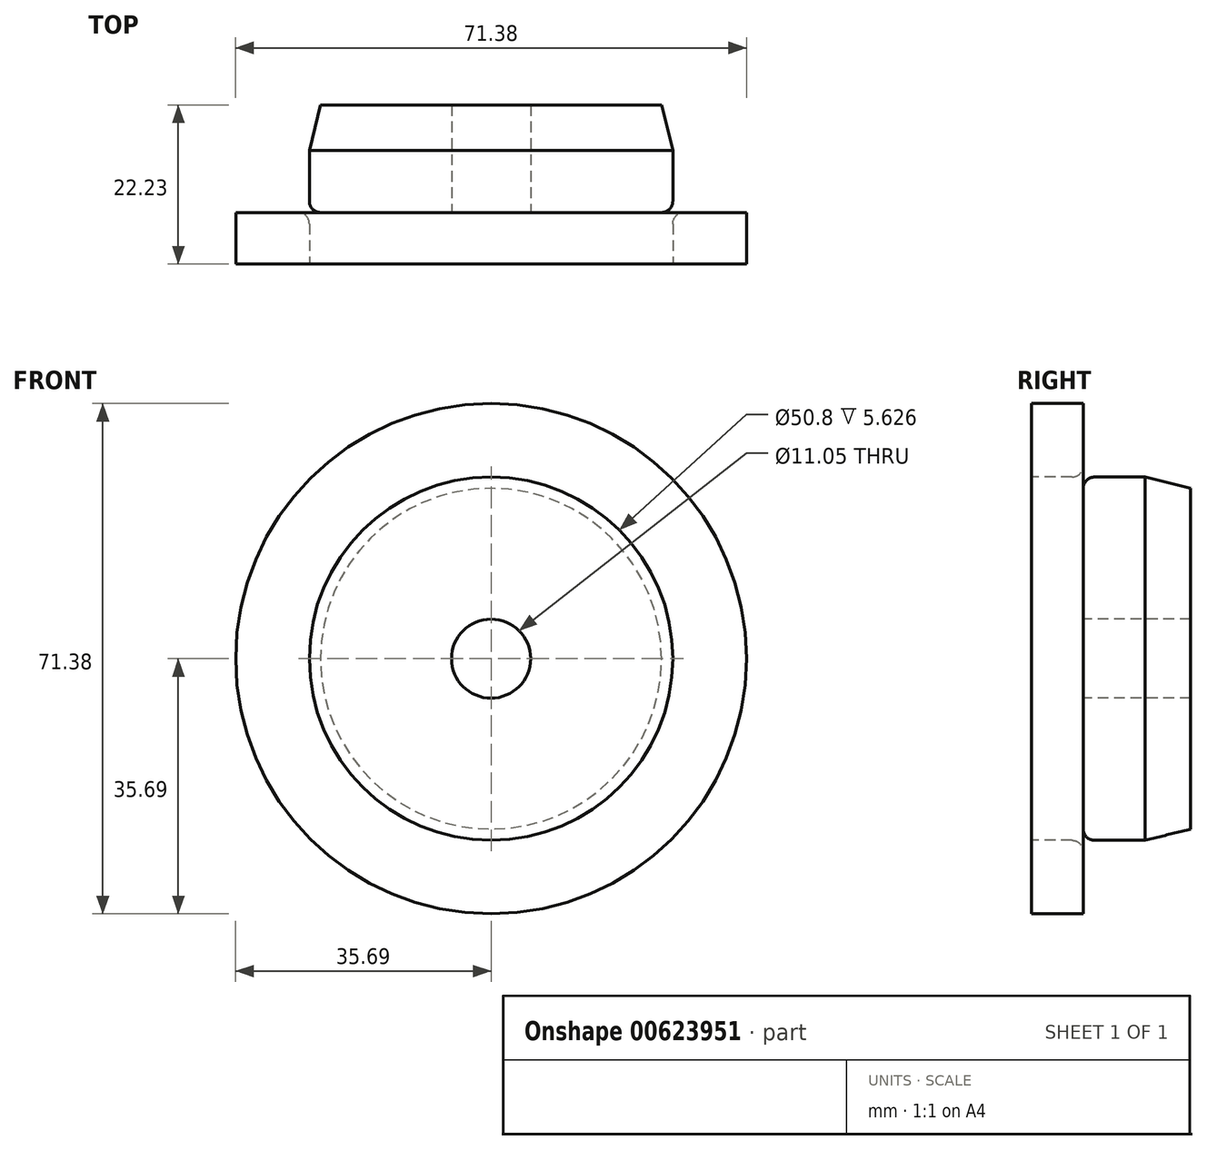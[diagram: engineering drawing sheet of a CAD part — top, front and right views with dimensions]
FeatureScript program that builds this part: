
annotation { "Feature Type Name" : "Feature", "Feature Type Description" : "" }
export const myFeature = defineFeature(function(context is Context, id is Id, definition is map)
    precondition{}
    {
        {
            var Q0;
            Q0=qCreatedBy(makeId("Right.planeOp"),FACE);
            var sketch = newSketch(context, id + "F0", { "sketchPlane" : qUnion([Q0])});
            skLineSegment(sketch, "E0", {"start": v(0, 0) * mm, "end": v(22.23, 0) * mm});
            skLineSegment(sketch, "E1.bottom", {"start": v(0, 5.52) * mm, "end": v(7.21, 5.52) * mm});
            skLineSegment(sketch, "E1.top", {"start": v(0, 35.69) * mm, "end": v(7.21, 35.69) * mm});
            skLineSegment(sketch, "E1.left", {"start": v(0, 5.52) * mm, "end": v(0, 35.69) * mm});
            skLineSegment(sketch, "E1.right", {"start": v(7.21, 5.52) * mm, "end": v(7.21, 35.69) * mm});
            skLineSegment(sketch, "E2.bottom", {"start": v(0, 5.52) * mm, "end": v(22.23, 5.52) * mm});
            skLineSegment(sketch, "E2.top", {"start": v(0, 25.4) * mm, "end": v(22.23, 25.4) * mm});
            skLineSegment(sketch, "E2.left", {"start": v(0, 5.52) * mm, "end": v(0, 25.4) * mm});
            skLineSegment(sketch, "E2.right", {"start": v(22.23, 5.52) * mm, "end": v(22.23, 25.4) * mm});
            skLineSegment(sketch, "E3.MirrorCS", {"start": v(0, -5.52) * mm, "end": v(7.21, -5.52) * mm});
            skLineSegment(sketch, "E4.MirrorCS", {"start": v(7.21, -5.52) * mm, "end": v(7.21, -35.69) * mm});
            skLineSegment(sketch, "E5.MirrorCS", {"start": v(0, -5.52) * mm, "end": v(22.23, -5.52) * mm});
            skLineSegment(sketch, "E6.MirrorCS", {"start": v(0, -5.52) * mm, "end": v(0, -35.69) * mm});
            skLineSegment(sketch, "E7.MirrorCS", {"start": v(0, -25.4) * mm, "end": v(22.23, -25.4) * mm});
            skLineSegment(sketch, "E8.MirrorCS", {"start": v(0, -35.69) * mm, "end": v(7.21, -35.69) * mm});
            skLineSegment(sketch, "E9.MirrorCS", {"start": v(22.23, -5.52) * mm, "end": v(22.23, -25.4) * mm});
            skLineSegment(sketch, "E10.MirrorCS", {"start": v(0, -5.52) * mm, "end": v(0, -25.4) * mm});
            skSolve(sketch);
        }
        {
            var Q0;
            {var subQ5=sQuery(id+"F0.wireOp",EDGE,"E2.right");Q0=makeQuery(id+"F0.imprint","IMPRINT",FACE,{"disambiguationData":[TD([[makeQuery(id+"F0.imprint","IMPRINT",EDGE,{"derivedFrom":subQ5}),1.0]])]});}
            var Q1;
            {var subQ5=sQuery(id+"F0.wireOp",EDGE,"E2.left");Q1=makeQuery(id+"F0.imprint","IMPRINT",FACE,{"disambiguationData":[TD([[makeQuery(id+"F0.imprint","IMPRINT",EDGE,{"derivedFrom":subQ5}),-1.0]])]});}
            var Q2;
            {var subQ0=sQuery(id+"F0.wireOp",EDGE,"E1.top");Q2=makeQuery(id+"F0.imprint","IMPRINT",FACE,{"disambiguationData":[TD([[makeQuery(id+"F0.imprint","IMPRINT",EDGE,{"derivedFrom":subQ0}),-1.0]])]});}
            var Q3;
            Q3=sQuery(id+"F0.wireOp",EDGE,"E0");
            revolve(context, id + "F1", {"entities" : qUnion([Q0, Q1, Q2]), "axis" : qUnion([Q3]), "revolveType" : RevolveType.FULL});
        }
        {
            var Q0;
            Q0=makeQuery(id+"F1.opRevolve","SWEPT_EDGE",EDGE,{"disambiguationData":[OSD([sQuery(id+"F0.wireOp",EDGE,"E1.right"),sQuery(id+"F0.wireOp",EDGE,"E2.top")])]});
            fillet(context, id + "F2", {"entities" : qUnion([Q0]), "radius" : 1.59 * mm, "tangentPropagation" : true, "allowEdgeOverflow" : false});
        }
        {
            var Q0;
            Q0=makeQuery(id+"F1.opRevolve","SWEPT_EDGE",EDGE,{"disambiguationData":[OSD([sQuery(id+"F0.wireOp",EDGE,"E2.top"),sQuery(id+"F0.wireOp",EDGE,"E2.right")])]});
            chamfer(context, id + "F3", {"entities" : qUnion([Q0]), "chamferType" : ChamferType.TWO_OFFSETS, "width1" : 6.35 * mm, "oppositeDirection" : false, "width2" : 1.57 * mm, "tangentPropagation" : true});
        }
    });
